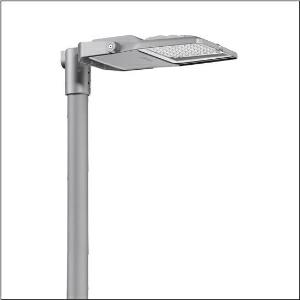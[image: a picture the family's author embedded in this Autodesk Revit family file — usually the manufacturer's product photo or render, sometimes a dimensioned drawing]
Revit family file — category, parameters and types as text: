
# Revit family: floodlight_fl_21_iq_mini___pl61_5xa7772d4c3a_23c5
name_source: partatom
category: Lighting Fixtures
units: mm (PartAtom-declared; Revit-internal decimal feet)

## family parameters
Cut with Voids When Loaded = No
Host = Face
Light Source = No
Part Type = Normal
Room Calculation Point = No
Round Connector Dimension = Use Diameter
Shared = No

## types (1)
- --- (1 x LED, 18260 lm, 143 W, 4000K)
    Apparent Load = 143 VA
    CIE Flux Codes = 33 65 98 100 100
    Color Rendering = 70
    Color Temperature = 4000K
    Default Elevation = 1800 mm
    Description = Floodlight FL 21 iQ mini, floodlight, primary light control with lens, of PMMA, primary optical cover: protective disc, of toughened safety glass, transparent, light distribution: PL61, light emission: direct distribution, installation type: surface-mounted, LED, High Power LED, rated luminous flux: 18.260lm, luminous efficacy: 128lm/W, light colour: 740, colour temperature: 4000K, control: Auto-Match, Temp-Guard, Night-Set, Smart-Wire, Desk-Remote (wireless, voltage-free reading and setting of iQ features in the workshop via application-optimized NFC function/RFID function), optimised constant luminous flux control (CLO 2.0), Light-Fading, Lumen-Switch, with terminal, 6-pole, mains connection: 220..240V, AC, 50/60Hz, start of lifetime: 143W, end of service life: 152W, reduction: 61W, luminaire housing, of diecast aluminium, powder-coated, Siteco® metallic grey (DB 702S), corrosivity category C5 mid according to DIN EN ISO 12944, sealing non-destructively replaceable, please order mast flange separately, mast bracket, of steel, galvanised, powder-coated, protection rating (complete): IP66, insulation class (complete): insulation class II (safety insulation), certification: CE, ENEC, VDE, protection symbol: D, impact resistance: IK08, permissible operating ambient temperature: -40..+40°C, permissible operating ambient temperature for outdoor applications: -40..+50°C, standard: DIN EN 12944, LABS conformity tested according to VDMA 24364:2018-05, packaging unit: 1 piece

Light Distribution: PL61
    Height = 70 mm
    Lamp = 1 x LED
    Lamp Light Flux = 18260 lm
    Lamp Power = 143 W
    Lamp count = 1
    Length = 485 mm
    Luminous efficacy = 128 lm/W
    Manufacturer = Siteco
    ModVariant = No
    Model = 5XA7772D4C3A
    Number of Poles = 1
    OnlyDefault = Yes
    Power Factor = 1
    Product Name = Floodlight FL 21 iQ mini | PL61
    Product group = floodlight | pylon annexe
    ProductGroupID = 6200
    Protection Class = Protection class II
    Protection Degree = IP 66
    RLX_Detail_Level = 1
    RLX_Emergency_Light_Flux = 0 lm
    RLX_Emergency_Type = 0
    RLX_Emergency_Type_DB = No
    RlxData = <blob elided: 101777 chars, md5=984f4a12>
    Socket = socket
    Standby Power = 0 W
    System Light Flux = 18260 lm
    System Power = 143 W
    Type Comments = factory setting: luminous flux: 100 % | dim-lin: 254 | 730 mA
    Type Image = l_1007125.jpg
    URL = http://relux.com
    VarID = @adj_105375
    Voltage = 0 V
    Weight = 0.00 kg
    Width = 337 mm

## geometry (parser evidence)
native form markers: Blend x4, Sweep x14
no freeform markers — native parametric forms only
